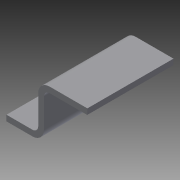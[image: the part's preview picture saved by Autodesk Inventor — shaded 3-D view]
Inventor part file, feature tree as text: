
AUTODESK INVENTOR PART (.ipt)
format: ipt  version: 2015 SP1 (Build 190203100, 203)  size: 92,672 bytes
history: native  units: in
note: dims shown in document units (in); Inventor stores cm internally (conversion verified against a paired STEP export)
features: extrude x1
ambient origin geometry x8: Origin, YZ Plane, XZ Plane, XY Plane, X Axis, Y Axis, Z Axis, Center Point
bodies: Solid1 (feature_tree)
feature tree (1):
  extrude  "Extrusion1"  Depth=1.1811in TaperAngle=0.0deg
